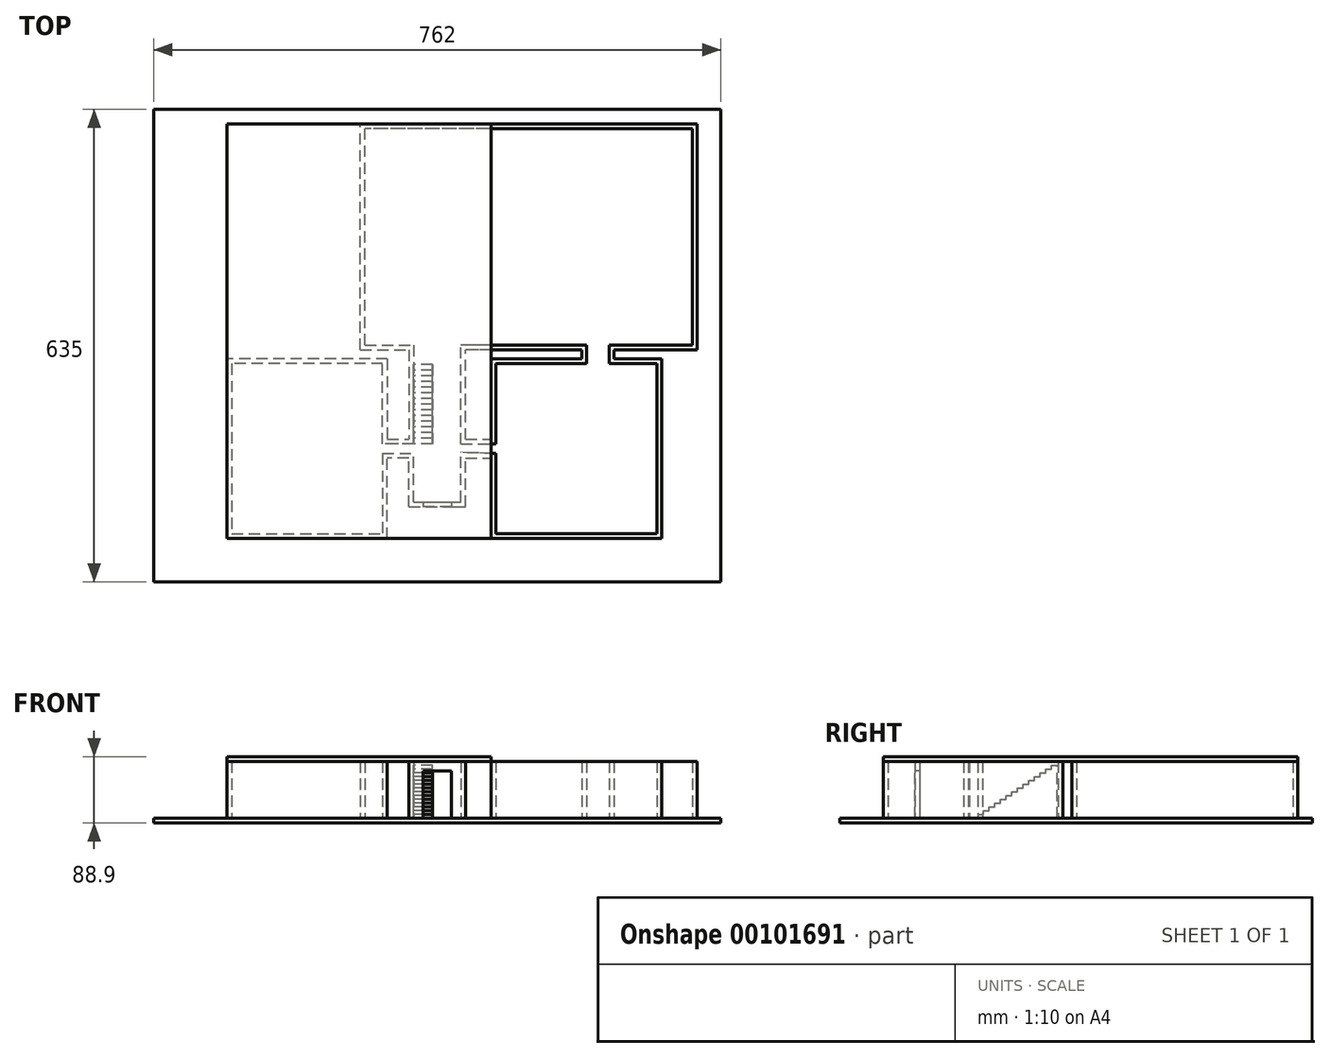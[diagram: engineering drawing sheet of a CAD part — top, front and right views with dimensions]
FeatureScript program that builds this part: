
annotation { "Feature Type Name" : "Feature", "Feature Type Description" : "" }
export const myFeature = defineFeature(function(context is Context, id is Id, definition is map)
    precondition{}
    {
        {
            var Q0;
            Q0=qCreatedBy(makeId("Top.planeOp"),FACE);
            var sketch = newSketch(context, id + "F0", { "sketchPlane" : qUnion([Q0])});
            skLineSegment(sketch, "E0.bottom", {"start": v(-322.44, 454.68) * mm, "end": v(439.56, 454.68) * mm});
            skLineSegment(sketch, "E0.top", {"start": v(-322.44, -180.32) * mm, "end": v(439.56, -180.32) * mm});
            skLineSegment(sketch, "E0.left", {"start": v(-322.44, 454.68) * mm, "end": v(-322.44, -180.32) * mm});
            skLineSegment(sketch, "E0.right", {"start": v(439.56, 454.68) * mm, "end": v(439.56, -180.32) * mm});
            skSolve(sketch);
        }
        {
            var Q0;
            Q0 = qSketchRegion(id + "F0", true);
            extrude(context, id + "F1", {"entities" : qUnion([Q0]), "depth" : 6.35 * mm});
        }
        {
            var Q0;
            Q0=makeQuery(id+"F1.opExtrude","CAP_FACE",FACE,{"disambiguationData":[OSD([sQuery(id+"F0.wireOp",EDGE,"E0.bottom"),sQuery(id+"F0.wireOp",EDGE,"E0.top"),sQuery(id+"F0.wireOp",EDGE,"E0.left"),sQuery(id+"F0.wireOp",EDGE,"E0.right")])],"isStart":false});
            var sketch = newSketch(context, id + "F2", { "sketchPlane" : qUnion([Q0])});
            skPoint(sketch, "E1.startSnap0", {"position": v(58.56, 454.68) * mm});
            skLineSegment(sketch, "E2", {"start": v(130.75, -122.19) * mm, "end": v(360.44, -122.19) * mm});
            skLineSegment(sketch, "E3", {"start": v(360.44, -122.19) * mm, "end": v(360.44, 119.11) * mm});
            skLineSegment(sketch, "E4", {"start": v(-8.49, 119.11) * mm, "end": v(-223.94, 119.11) * mm});
            skLineSegment(sketch, "E5", {"start": v(-223.94, 119.11) * mm, "end": v(-223.94, -122.19) * mm});
            skLineSegment(sketch, "E6", {"start": v(-223.94, -122.19) * mm, "end": v(-8.49, -122.19) * mm});
            skLineSegment(sketch, "E7", {"start": v(20.46, -79.42) * mm, "end": v(96.66, -79.42) * mm});
            skLineSegment(sketch, "E8.0", {"start": v(-14.84, -7.89) * mm, "end": v(-14.84, -115.84) * mm});
            skLineSegment(sketch, "E8.1", {"start": v(-14.84, 4.81) * mm, "end": v(-14.84, 112.76) * mm});
            skLineSegment(sketch, "E8.2", {"start": v(-14.84, 112.76) * mm, "end": v(-217.6, 112.76) * mm});
            skLineSegment(sketch, "E8.3", {"start": v(-217.6, 112.76) * mm, "end": v(-217.6, -115.84) * mm});
            skLineSegment(sketch, "E8.4", {"start": v(-217.6, -115.84) * mm, "end": v(-14.84, -115.84) * mm});
            skLineSegment(sketch, "E9.0", {"start": v(137.1, 112.76) * mm, "end": v(137.1, 4.81) * mm});
            skLineSegment(sketch, "E9.1", {"start": v(137.1, -7.89) * mm, "end": v(137.1, -115.84) * mm});
            skLineSegment(sketch, "E9.2", {"start": v(137.1, -115.84) * mm, "end": v(354.09, -115.84) * mm});
            skLineSegment(sketch, "E9.3", {"start": v(354.09, -115.84) * mm, "end": v(354.09, 112.76) * mm});
            skLineSegment(sketch, "E10.0", {"start": v(26.8, -73.07) * mm, "end": v(26.8, -7.89) * mm});
            skLineSegment(sketch, "E10.1", {"start": v(26.8, -73.07) * mm, "end": v(90.3, -73.07) * mm});
            skLineSegment(sketch, "E10.2", {"start": v(90.3, -73.07) * mm, "end": v(90.3, -6.57) * mm});
            skLineSegment(sketch, "E11", {"start": v(-8.49, -122.19) * mm, "end": v(-8.49, -14.24) * mm});
            skLineSegment(sketch, "E12", {"start": v(-8.49, 119.11) * mm, "end": v(-8.49, 11.16) * mm});
            skLineSegment(sketch, "E13", {"start": v(20.46, -79.42) * mm, "end": v(20.46, -14.24) * mm});
            skLineSegment(sketch, "E14", {"start": v(20.46, -14.24) * mm, "end": v(-8.49, -14.24) * mm});
            skLineSegment(sketch, "E15", {"start": v(26.8, 4.81) * mm, "end": v(-14.84, 4.81) * mm});
            skLineSegment(sketch, "E16", {"start": v(-8.49, 11.16) * mm, "end": v(20.46, 11.16) * mm});
            skLineSegment(sketch, "E17", {"start": v(-14.84, -7.89) * mm, "end": v(26.8, -7.89) * mm});
            skLineSegment(sketch, "E18", {"start": v(96.66, 11.16) * mm, "end": v(130.75, 11.16) * mm});
            skLineSegment(sketch, "E19", {"start": v(130.75, 11.16) * mm, "end": v(130.75, 119.11) * mm});
            skLineSegment(sketch, "E20", {"start": v(96.66, -79.42) * mm, "end": v(96.66, -14.24) * mm});
            skLineSegment(sketch, "E21", {"start": v(96.66, -14.24) * mm, "end": v(130.75, -14.24) * mm});
            skLineSegment(sketch, "E22", {"start": v(130.75, -14.24) * mm, "end": v(130.75, -122.19) * mm});
            skLineSegment(sketch, "E23", {"start": v(137.1, -7.89) * mm, "end": v(90.3, -6.57) * mm});
            skLineSegment(sketch, "E24", {"start": v(90.3, 4.81) * mm, "end": v(137.1, 4.81) * mm});
            skLineSegment(sketch, "E25", {"start": v(96.66, 11.16) * mm, "end": v(96.66, 131.43) * mm});
            skPoint(sketch, "E26.endSnap0", {"position": v(245.6, 119.11) * mm});
            skLineSegment(sketch, "E27", {"start": v(408.07, 131.43) * mm, "end": v(408.07, 434.94) * mm});
            skLineSegment(sketch, "E28", {"start": v(408.07, 434.94) * mm, "end": v(-44.96, 434.94) * mm});
            skLineSegment(sketch, "E29.1", {"start": v(401.72, 428.6) * mm, "end": v(-38.61, 428.6) * mm});
            skLineSegment(sketch, "E29.5", {"start": v(401.72, 137.78) * mm, "end": v(401.72, 428.6) * mm});
            skLineSegment(sketch, "E30", {"start": v(-44.96, 131.43) * mm, "end": v(20.46, 131.43) * mm});
            skLineSegment(sketch, "E31", {"start": v(20.46, 131.43) * mm, "end": v(20.46, 11.16) * mm});
            skLineSegment(sketch, "E32", {"start": v(-38.61, 137.78) * mm, "end": v(26.8, 137.78) * mm});
            skLineSegment(sketch, "E33", {"start": v(26.8, 137.78) * mm, "end": v(26.8, 4.81) * mm});
            skLineSegment(sketch, "E34", {"start": v(90.3, 4.81) * mm, "end": v(90.3, 137.78) * mm});
            skLineSegment(sketch, "E35", {"start": v(360.44, 119.11) * mm, "end": v(296.1, 119.11) * mm});
            skLineSegment(sketch, "E36", {"start": v(130.75, 119.11) * mm, "end": v(252.67, 119.11) * mm});
            skLineSegment(sketch, "E37", {"start": v(252.67, 119.11) * mm, "end": v(252.67, 131.43) * mm});
            skLineSegment(sketch, "E38", {"start": v(296.1, 119.11) * mm, "end": v(296.1, 131.43) * mm});
            skLineSegment(sketch, "E39", {"start": v(296.1, 131.43) * mm, "end": v(408.07, 131.43) * mm});
            skLineSegment(sketch, "E40", {"start": v(252.67, 131.43) * mm, "end": v(96.66, 131.43) * mm});
            skLineSegment(sketch, "E41", {"start": v(354.09, 112.76) * mm, "end": v(289.75, 112.76) * mm});
            skLineSegment(sketch, "E42", {"start": v(137.1, 112.76) * mm, "end": v(259.02, 112.76) * mm});
            skLineSegment(sketch, "E43", {"start": v(259.02, 112.76) * mm, "end": v(259.02, 137.78) * mm});
            skLineSegment(sketch, "E44", {"start": v(289.75, 112.76) * mm, "end": v(289.75, 137.78) * mm});
            skLineSegment(sketch, "E45", {"start": v(289.75, 137.78) * mm, "end": v(401.72, 137.78) * mm});
            skLineSegment(sketch, "E46", {"start": v(259.02, 137.78) * mm, "end": v(90.3, 137.78) * mm});
            skLineSegment(sketch, "E47", {"start": v(-44.96, 131.43) * mm, "end": v(-44.96, 434.94) * mm});
            skLineSegment(sketch, "E48", {"start": v(-38.61, 137.78) * mm, "end": v(-38.61, 428.6) * mm});
            skSolve(sketch);
        }
        {
            var Q0;
            Q0 = qSketchRegion(id + "F2", true);
            var Q1;
            Q1=makeQuery(id+"F2.imprint","IMPRINT",FACE,{"disambiguationData":[TD([[makeQuery(id+"F2.imprint","IMPRINT",EDGE,{"derivedFrom":sQuery(id+"F2.wireOp",EDGE,"E9.0")}),-1.0]])]});
            extrude(context, id + "F3", {"entities" : qUnion([Q0, Q1]), "operationType" : NewBodyOperationType.ADD, "depth" : 76.2 * mm});
        }
        {
            var Q0;
            {var subQ0=sQuery(id+"F0.wireOp",EDGE,"E0.bottom");var subQ1=sQuery(id+"F0.wireOp",EDGE,"E0.right");var subQ2=sQuery(id+"F0.wireOp",EDGE,"E0.top");var subQ3=sQuery(id+"F0.wireOp",EDGE,"E0.left");Q0=makeQuery(id+"F3.boolean.opBoolean","SPLIT",FACE,{"disambiguationData":[TD([makeQuery(id+"F1.opExtrude","SWEPT_FACE",FACE,{"disambiguationData":[OSD([subQ0])]})])],"derivedFrom":makeQuery(id+"F1.opExtrude","CAP_FACE",FACE,{"disambiguationData":[OSD([subQ0,subQ2,subQ3,subQ1])],"isStart":false})});}
            var sketch = newSketch(context, id + "F4", { "sketchPlane" : qUnion([Q0])});
            skSolve(sketch);
        }
        {
            var Q0;
            Q0=makeQuery(id+"F3.opExtrude","SWEPT_FACE",FACE,{"disambiguationData":[OSD([sQuery(id+"F2.wireOp",EDGE,"E7")])]});
            var sketch = newSketch(context, id + "F5", { "sketchPlane" : qUnion([Q0])});
            skLineSegment(sketch, "E49", {"start": v(58.56, 6.35) * mm, "end": v(20.46, 6.35) * mm});
            skLineSegment(sketch, "E50", {"start": v(20.46, 6.35) * mm, "end": v(58.56, 6.35) * mm});
            skLineSegment(sketch, "E51", {"start": v(96.66, 6.35) * mm, "end": v(58.56, 6.35) * mm});
            skLineSegment(sketch, "E52", {"start": v(77.6, 6.35) * mm, "end": v(77.6, 69.85) * mm});
            skLineSegment(sketch, "E53", {"start": v(77.6, 69.85) * mm, "end": v(39.5, 69.85) * mm});
            skPoint(sketch, "E53.endSnap0", {"position": v(39.5, 6.35) * mm});
            skLineSegment(sketch, "E54", {"start": v(39.5, 69.85) * mm, "end": v(39.5, 6.35) * mm});
            skSolve(sketch);
        }
        {
            var Q0;
            Q0 = qSketchRegion(id + "F5", true);
            extrude(context, id + "F6", {"entities" : qUnion([Q0]), "operationType" : NewBodyOperationType.REMOVE, "oppositeDirection" : true, "depth" : 25.4 * mm});
        }
        {
            var Q0;
            Q0=makeQuery(id+"F3.opExtrude","SWEPT_FACE",FACE,{"disambiguationData":[OSD([sQuery(id+"F2.wireOp",EDGE,"E33")])]});
            var sketch = newSketch(context, id + "F7", { "sketchPlane" : qUnion([Q0])});
            skLineSegment(sketch, "E55", {"start": v(4.81, 6.35) * mm, "end": v(4.81, 11.43) * mm});
            skLineSegment(sketch, "E56", {"start": v(4.81, 11.43) * mm, "end": v(12.43, 11.43) * mm});
            skLineSegment(sketch, "E57", {"start": v(12.43, 11.43) * mm, "end": v(12.43, 16.51) * mm});
            skLineSegment(sketch, "E58", {"start": v(12.43, 16.51) * mm, "end": v(20.05, 16.51) * mm});
            skLineSegment(sketch, "E59", {"start": v(20.05, 16.51) * mm, "end": v(20.05, 21.6) * mm});
            skLineSegment(sketch, "E60", {"start": v(20.05, 21.6) * mm, "end": v(27.67, 21.6) * mm});
            skLineSegment(sketch, "E61", {"start": v(27.67, 21.6) * mm, "end": v(27.67, 26.67) * mm});
            skLineSegment(sketch, "E62", {"start": v(27.67, 26.67) * mm, "end": v(35.3, 26.67) * mm});
            skLineSegment(sketch, "E63", {"start": v(35.3, 26.67) * mm, "end": v(35.3, 31.75) * mm});
            skLineSegment(sketch, "E64", {"start": v(35.3, 31.75) * mm, "end": v(42.91, 31.75) * mm});
            skLineSegment(sketch, "E65", {"start": v(42.91, 31.75) * mm, "end": v(42.91, 36.83) * mm});
            skLineSegment(sketch, "E66", {"start": v(42.91, 36.83) * mm, "end": v(50.53, 36.83) * mm});
            skLineSegment(sketch, "E67", {"start": v(50.53, 36.83) * mm, "end": v(50.53, 41.91) * mm});
            skLineSegment(sketch, "E68", {"start": v(50.53, 41.91) * mm, "end": v(58.15, 41.91) * mm});
            skLineSegment(sketch, "E69", {"start": v(58.15, 41.91) * mm, "end": v(58.15, 47) * mm});
            skLineSegment(sketch, "E70", {"start": v(58.15, 47) * mm, "end": v(65.77, 47) * mm});
            skLineSegment(sketch, "E71", {"start": v(65.77, 47) * mm, "end": v(65.77, 52.07) * mm});
            skLineSegment(sketch, "E72", {"start": v(65.77, 52.07) * mm, "end": v(73.4, 52.07) * mm});
            skLineSegment(sketch, "E73", {"start": v(73.4, 52.07) * mm, "end": v(73.4, 57.15) * mm});
            skLineSegment(sketch, "E74", {"start": v(73.4, 57.15) * mm, "end": v(81.01, 57.15) * mm});
            skLineSegment(sketch, "E75", {"start": v(81.01, 57.15) * mm, "end": v(81.01, 62.23) * mm});
            skLineSegment(sketch, "E76", {"start": v(81.01, 62.23) * mm, "end": v(88.63, 62.23) * mm});
            skLineSegment(sketch, "E77", {"start": v(88.63, 62.23) * mm, "end": v(88.63, 67.31) * mm});
            skLineSegment(sketch, "E78", {"start": v(88.63, 67.31) * mm, "end": v(96.25, 67.31) * mm});
            skLineSegment(sketch, "E79", {"start": v(96.25, 67.31) * mm, "end": v(96.25, 72.4) * mm});
            skLineSegment(sketch, "E80", {"start": v(96.25, 72.4) * mm, "end": v(103.87, 72.4) * mm});
            skLineSegment(sketch, "E81", {"start": v(103.87, 72.4) * mm, "end": v(103.87, 77.47) * mm});
            skLineSegment(sketch, "E82", {"start": v(103.87, 77.47) * mm, "end": v(111.5, 77.47) * mm});
            skLineSegment(sketch, "E83", {"start": v(4.81, 6.35) * mm, "end": v(111.5, 6.35) * mm});
            skLineSegment(sketch, "E84", {"start": v(111.5, 6.35) * mm, "end": v(111.5, 77.47) * mm});
            skLineSegment(sketch, "E85", {"start": v(111.5, 6.35) * mm, "end": v(4.81, 6.35) * mm});
            skSolve(sketch);
        }
        {
            var Q0;
            Q0 = qSketchRegion(id + "F7", true);
            extrude(context, id + "F8", {"entities" : qUnion([Q0]), "operationType" : NewBodyOperationType.ADD, "depth" : 25.4 * mm});
        }
        {
            var Q0;
            Q0=makeQuery(id+"F3.opExtrude","CAP_FACE",FACE,{"disambiguationData":[OSD([sQuery(id+"F2.wireOp",EDGE,"E2"),sQuery(id+"F2.wireOp",EDGE,"E3"),sQuery(id+"F2.wireOp",EDGE,"E4"),sQuery(id+"F2.wireOp",EDGE,"E5"),sQuery(id+"F2.wireOp",EDGE,"E6"),sQuery(id+"F2.wireOp",EDGE,"E7"),sQuery(id+"F2.wireOp",EDGE,"E8.0"),sQuery(id+"F2.wireOp",EDGE,"E8.1"),sQuery(id+"F2.wireOp",EDGE,"E8.2"),sQuery(id+"F2.wireOp",EDGE,"E8.3"),sQuery(id+"F2.wireOp",EDGE,"E8.4"),sQuery(id+"F2.wireOp",EDGE,"E9.1"),sQuery(id+"F2.wireOp",EDGE,"E9.2"),sQuery(id+"F2.wireOp",EDGE,"E9.3"),sQuery(id+"F2.wireOp",EDGE,"E10.0"),sQuery(id+"F2.wireOp",EDGE,"E10.1"),sQuery(id+"F2.wireOp",EDGE,"E10.2"),sQuery(id+"F2.wireOp",EDGE,"E11"),sQuery(id+"F2.wireOp",EDGE,"E12"),sQuery(id+"F2.wireOp",EDGE,"E13"),sQuery(id+"F2.wireOp",EDGE,"E14"),sQuery(id+"F2.wireOp",EDGE,"E15"),sQuery(id+"F2.wireOp",EDGE,"E16"),sQuery(id+"F2.wireOp",EDGE,"E17"),sQuery(id+"F2.wireOp",EDGE,"E20"),sQuery(id+"F2.wireOp",EDGE,"E21"),sQuery(id+"F2.wireOp",EDGE,"E22"),sQuery(id+"F2.wireOp",EDGE,"E23"),sQuery(id+"F2.wireOp",EDGE,"E27"),sQuery(id+"F2.wireOp",EDGE,"E28"),sQuery(id+"F2.wireOp",EDGE,"E29.1"),sQuery(id+"F2.wireOp",EDGE,"E29.5"),sQuery(id+"F2.wireOp",EDGE,"E30"),sQuery(id+"F2.wireOp",EDGE,"E31"),sQuery(id+"F2.wireOp",EDGE,"E32"),sQuery(id+"F2.wireOp",EDGE,"E33"),sQuery(id+"F2.wireOp",EDGE,"E35"),sQuery(id+"F2.wireOp",EDGE,"E38"),sQuery(id+"F2.wireOp",EDGE,"E39"),sQuery(id+"F2.wireOp",EDGE,"E41"),sQuery(id+"F2.wireOp",EDGE,"E44"),sQuery(id+"F2.wireOp",EDGE,"E45"),sQuery(id+"F2.wireOp",EDGE,"E47"),sQuery(id+"F2.wireOp",EDGE,"E48")])],"isStart":false});
            var sketch = newSketch(context, id + "F9", { "sketchPlane" : qUnion([Q0])});
            skLineSegment(sketch, "E86.bottom", {"start": v(-223.94, -122.19) * mm, "end": v(130.75, -122.19) * mm});
            skLineSegment(sketch, "E86.top", {"start": v(-223.94, 434.94) * mm, "end": v(130.75, 434.94) * mm});
            skLineSegment(sketch, "E86.left", {"start": v(-223.94, -122.19) * mm, "end": v(-223.94, 434.94) * mm});
            skLineSegment(sketch, "E86.right", {"start": v(130.75, -122.19) * mm, "end": v(130.75, 434.94) * mm});
            skSolve(sketch);
        }
        {
            var Q0;
            Q0 = qSketchRegion(id + "F9", true);
            extrude(context, id + "F10", {"entities" : qUnion([Q0]), "depth" : 6.35 * mm});
        }
    });
